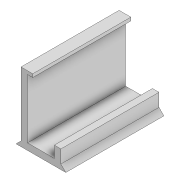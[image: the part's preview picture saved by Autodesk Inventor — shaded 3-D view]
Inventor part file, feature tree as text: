
AUTODESK INVENTOR PART (.ipt)
format: ipt  version: 2021 (Build 250183000, 183)  size: 190,464 bytes
history: native  units: mm
features: extrude x9, sketch x9, projected_geometry x5, mirror x2
ambient origin geometry x8: Origin, YZ Plane, XZ Plane, XY Plane, X Axis, Y Axis, Z Axis, Center Point
bodies: Volumenkörper1 (feature_tree)
feature tree (25):
  extrude  "Extrusion1"  Depth=30.0mm
  extrude  "Extrusion2"  Depth=12.2mm
  extrude  "Extrusion3"  Depth=2.0mm TaperAngle=0.0deg
  extrude  "Extrusion4"  Depth=2.0mm TaperAngle=0.0deg
  extrude  "Extrusion6"  Depth=0.6mm
  mirror  "Spiegeln1"
  extrude  "Extrusion7"  Depth=14.6mm
  extrude  "Extrusion8"  TaperAngle=0.0deg  [1 undecoded]
  mirror  "Spiegeln2"
  extrude  "Extrusion10"  Depth=2.0mm
  extrude  "Extrusion11"  Depth=1.5mm
  sketch  "Skizze1"  dims[d0=8.2mm d1=30.0mm]
  sketch  "Skizze2"  dims[d2=12.2mm d3=34.0mm]
  projected_geometry  "Projizierte Kontur1"
  sketch  "Skizze3"  dims[d4=18.1mm d5=0.0mm d6=2.0mm d7=0.0mm]
  projected_geometry  "Projizierte Kontur2"
  sketch  "Skizze4"  dims[d8=3.5mm d9=2.0mm d10=0.0mm]
  sketch  "Skizze6"  dims[d11=0.6mm d12=0.6mm]
  sketch  "Skizze7"  dims[d13=1.0mm d14=0.0mm d30=14.6mm]
  projected_geometry  "Projizierte Kontur3"
  sketch  "Skizze8"  dims[d31=0.0mm d32=0.0mm d33=0.0mm d34=0.0mm]
  projected_geometry  "Projizierte Kontur4"
  sketch  "Skizze10"  dims[d35=2.0mm d36=0.0mm d44=1.5mm]
  sketch  "Skizze11"  dims[d45=1.5mm d46=1.5mm d47=1.5mm d48=10.0mm d49=0.0mm d50=0.4mm d51=0.0mm]
  projected_geometry  "Projizierte Kontur5"
note: 1 required parameter value undecoded (feature->parameter linkage not recoverable at this tier; creation-order binding heuristic only, values carry confidence <= 0.55)
